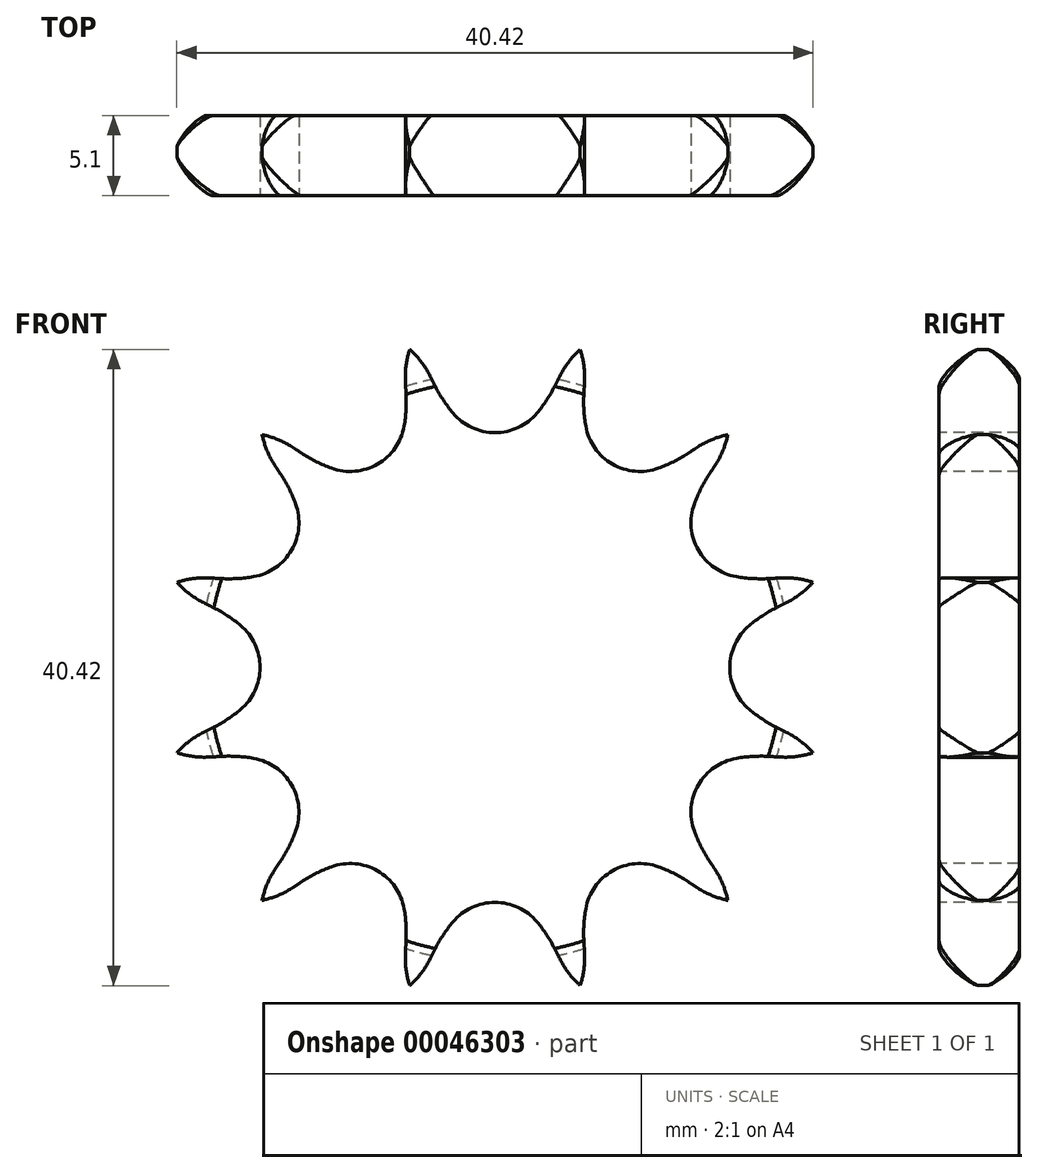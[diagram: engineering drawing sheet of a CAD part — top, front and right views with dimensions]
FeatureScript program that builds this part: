
annotation { "Feature Type Name" : "Feature", "Feature Type Description" : "" }
export const myFeature = defineFeature(function(context is Context, id is Id, definition is map)
    precondition{}
    {
        {
            var Q0;
            Q0=qCreatedBy(makeId("Right.planeOp"),FACE);
            var sketch = newSketch(context, id + "F0", { "sketchPlane" : qUnion([Q0])});
            skLineSegment(sketch, "E0", {"start": v(0, 0) * mm, "end": v(5.1, 0) * mm, "construction": true});
            skLineSegment(sketch, "E1", {"start": v(0, 21) * mm, "end": v(5.1, 21) * mm});
            skLineSegment(sketch, "E2", {"start": v(5.1, 21) * mm, "end": v(5.1, 15) * mm});
            skLineSegment(sketch, "E3", {"start": v(5.1, 15) * mm, "end": v(5.1, 15) * mm});
            skLineSegment(sketch, "E4", {"start": v(5.1, 15) * mm, "end": v(5.1, 0) * mm});
            skLineSegment(sketch, "E5", {"start": v(0, 0) * mm, "end": v(0, 21) * mm});
            skLineSegment(sketch, "E6.0.MirrorCS", {"start": v(0, -21) * mm, "end": v(5.1, -21) * mm});
            skLineSegment(sketch, "E6.1.MirrorCS", {"start": v(5.1, -21) * mm, "end": v(5.1, -15) * mm});
            skLineSegment(sketch, "E6.3.MirrorCS", {"start": v(5.1, -15) * mm, "end": v(5.1, 0) * mm});
            skLineSegment(sketch, "E6.4.MirrorCS", {"start": v(5.1, -15) * mm, "end": v(5.1, -15) * mm});
            skLineSegment(sketch, "E6.5.MirrorCS", {"start": v(0, 0) * mm, "end": v(0, -21) * mm});
            skLineSegment(sketch, "E7", {"start": v(0, 0) * mm, "end": v(5.1, 0) * mm});
            skSolve(sketch);
        }
        {
            var Q0;
            Q0=makeQuery(id+"F0.imprint","IMPRINT",FACE,{"disambiguationData":[TD([[makeQuery(id+"F0.imprint","IMPRINT",EDGE,{"derivedFrom":sQuery(id+"F0.wireOp",EDGE,"E1")}),-1.0]])]});
            var Q1;
            Q1=sQuery(id+"F0.wireOp",EDGE,"E0");
            revolve(context, id + "F1", {"entities" : qUnion([Q0]), "axis" : qUnion([Q1]), "revolveType" : RevolveType.FULL});
        }
        {
            var Q0;
            Q0=makeQuery(id+"F1.opRevolve","SWEPT_EDGE",EDGE,{"disambiguationData":[OSD([sQuery(id+"F0.wireOp",EDGE,"E1"),sQuery(id+"F0.wireOp",EDGE,"E5")])]});
            fillet(context, id + "F2", {"entities" : qUnion([Q0]), "radius" : 2.75 * mm, "tangentPropagation" : true, "rho" : 0.2, "crossSection" : FilletCrossSection.CONIC, "allowEdgeOverflow" : false});
        }
        {
            var Q0;
            Q0=makeQuery(id+"F1.opRevolve","SWEPT_EDGE",EDGE,{"disambiguationData":[OSD([sQuery(id+"F0.wireOp",EDGE,"E1"),sQuery(id+"F0.wireOp",EDGE,"E2")])]});
            fillet(context, id + "F3", {"entities" : qUnion([Q0]), "radius" : 2.25 * mm, "tangentPropagation" : true, "rho" : 0.2, "crossSection" : FilletCrossSection.CONIC, "allowEdgeOverflow" : false});
        }
        {
            var Q0;
            Q0=qCreatedBy(makeId("Front.planeOp"),FACE);
            var sketch = newSketch(context, id + "F4", { "sketchPlane" : qUnion([Q0])});
            skPoint(sketch, "E8.0", {"position": v(0, 0) * mm});
            skArc(sketch, "E9", {"start": v(2.67, 16.16) * mm, "mid": v(0, 21.88) * mm, "end": v(-2.67, 16.16) * mm, "construction": true});
            skLineSegment(sketch, "E10", {"start": v(0, 0) * mm, "end": v(7.32, 0) * mm, "construction": true});
            skArc(sketch, "E11", {"start": v(-2.67, 16.16) * mm, "mid": v(11.7, 26.86) * mm, "end": v(-3.81, 17.9) * mm, "construction": true});
            skLineSegment(sketch, "E12", {"start": v(4.9, 0.57) * mm, "end": v(-4.12, 18.5) * mm, "construction": true});
            skArc(sketch, "E13", {"start": v(-5.41, 20.2) * mm, "mid": v(-13.86, 12.42) * mm, "end": v(-4.12, 18.5) * mm, "construction": true});
            skLineSegment(sketch, "E14", {"start": v(0, 0) * mm, "end": v(-5.41, 20.2) * mm, "construction": true});
            skLineSegment(sketch, "E15", {"start": v(4.2, 21.93) * mm, "end": v(-3.81, 17.9) * mm, "construction": true});
            skLineSegment(sketch, "E16", {"start": v(0, 18.4) * mm, "end": v(4.2, 21.93) * mm, "construction": true});
            skLineSegment(sketch, "E17", {"start": v(0, 18.4) * mm, "end": v(72.06, 18.4) * mm, "construction": true});
            skLineSegment(sketch, "E18", {"start": v(0, 0) * mm, "end": v(0, 18.4) * mm, "construction": true});
            skCircle(sketch, "E19", {"center": v(0, 0) * mm, "radius": 18.4 * mm, "construction": true});
            skArc(sketch, "E20", {"start": v(-2.67, 16.16) * mm, "mid": v(0, 14.92) * mm, "end": v(2.67, 16.16) * mm});
            skArc(sketch, "E21.0.MirrorCS", {"start": v(4.12, 18.5) * mm, "mid": v(4.69, 19.42) * mm, "end": v(5.41, 20.2) * mm});
            skLineSegment(sketch, "E22.0.MirrorCS", {"start": v(3.81, 17.9) * mm, "end": v(4.12, 18.5) * mm});
            skArc(sketch, "E23.0.MirrorCS", {"start": v(3.81, 17.9) * mm, "mid": v(3.3, 17) * mm, "end": v(2.67, 16.16) * mm});
            skArc(sketch, "E24", {"start": v(-3.81, 17.9) * mm, "mid": v(-3.3, 17) * mm, "end": v(-2.67, 16.16) * mm});
            skArc(sketch, "E25", {"start": v(-4.12, 18.5) * mm, "mid": v(-4.69, 19.42) * mm, "end": v(-5.41, 20.2) * mm});
            skLineSegment(sketch, "E26", {"start": v(-3.81, 17.9) * mm, "end": v(-4.12, 18.5) * mm});
            skArc(sketch, "E27.1.0", {"start": v(-12.82, 13.97) * mm, "mid": v(-13.77, 14.47) * mm, "end": v(-14.8, 14.8) * mm});
            skLineSegment(sketch, "E27.1.1", {"start": v(-12.25, 13.6) * mm, "end": v(-12.82, 13.97) * mm});
            skArc(sketch, "E27.1.2", {"start": v(-12.25, 13.6) * mm, "mid": v(-11.35, 13.07) * mm, "end": v(-10.4, 12.66) * mm});
            skArc(sketch, "E27.1.3", {"start": v(-5.65, 17.4) * mm, "mid": v(-5.65, 16.37) * mm, "end": v(-5.77, 15.33) * mm});
            skLineSegment(sketch, "E27.1.4", {"start": v(-5.65, 17.4) * mm, "end": v(-5.69, 18.08) * mm});
            skArc(sketch, "E27.1.5", {"start": v(-5.69, 18.08) * mm, "mid": v(-5.65, 19.16) * mm, "end": v(-5.41, 20.2) * mm});
            skArc(sketch, "E27.1.6", {"start": v(-10.4, 12.66) * mm, "mid": v(-7.46, 12.92) * mm, "end": v(-5.77, 15.33) * mm});
            skArc(sketch, "E27.2.0", {"start": v(-18.08, 5.69) * mm, "mid": v(-19.16, 5.65) * mm, "end": v(-20.2, 5.41) * mm});
            skLineSegment(sketch, "E27.2.1", {"start": v(-17.4, 5.65) * mm, "end": v(-18.08, 5.69) * mm});
            skArc(sketch, "E27.2.2", {"start": v(-17.4, 5.65) * mm, "mid": v(-16.37, 5.65) * mm, "end": v(-15.33, 5.77) * mm});
            skArc(sketch, "E27.2.3", {"start": v(-13.6, 12.25) * mm, "mid": v(-13.07, 11.35) * mm, "end": v(-12.66, 10.4) * mm});
            skLineSegment(sketch, "E27.2.4", {"start": v(-13.6, 12.25) * mm, "end": v(-13.97, 12.82) * mm});
            skArc(sketch, "E27.2.5", {"start": v(-13.97, 12.82) * mm, "mid": v(-14.47, 13.77) * mm, "end": v(-14.8, 14.8) * mm});
            skArc(sketch, "E27.2.6", {"start": v(-15.33, 5.77) * mm, "mid": v(-12.92, 7.46) * mm, "end": v(-12.66, 10.4) * mm});
            skArc(sketch, "E27.3.0", {"start": v(-18.5, -4.12) * mm, "mid": v(-19.42, -4.69) * mm, "end": v(-20.2, -5.41) * mm});
            skLineSegment(sketch, "E27.3.1", {"start": v(-17.9, -3.81) * mm, "end": v(-18.5, -4.12) * mm});
            skArc(sketch, "E27.3.2", {"start": v(-17.9, -3.81) * mm, "mid": v(-17, -3.3) * mm, "end": v(-16.16, -2.67) * mm});
            skArc(sketch, "E27.3.3", {"start": v(-17.9, 3.81) * mm, "mid": v(-17, 3.3) * mm, "end": v(-16.16, 2.67) * mm});
            skLineSegment(sketch, "E27.3.4", {"start": v(-17.9, 3.81) * mm, "end": v(-18.5, 4.12) * mm});
            skArc(sketch, "E27.3.5", {"start": v(-18.5, 4.12) * mm, "mid": v(-19.42, 4.69) * mm, "end": v(-20.2, 5.41) * mm});
            skArc(sketch, "E27.3.6", {"start": v(-16.16, -2.67) * mm, "mid": v(-14.92, 0) * mm, "end": v(-16.16, 2.67) * mm});
            skArc(sketch, "E27.4.0", {"start": v(-13.97, -12.82) * mm, "mid": v(-14.47, -13.77) * mm, "end": v(-14.8, -14.8) * mm});
            skLineSegment(sketch, "E27.4.1", {"start": v(-13.6, -12.25) * mm, "end": v(-13.97, -12.82) * mm});
            skArc(sketch, "E27.4.2", {"start": v(-13.6, -12.25) * mm, "mid": v(-13.07, -11.35) * mm, "end": v(-12.66, -10.4) * mm});
            skArc(sketch, "E27.4.3", {"start": v(-17.4, -5.65) * mm, "mid": v(-16.37, -5.65) * mm, "end": v(-15.33, -5.77) * mm});
            skLineSegment(sketch, "E27.4.4", {"start": v(-17.4, -5.65) * mm, "end": v(-18.08, -5.69) * mm});
            skArc(sketch, "E27.4.5", {"start": v(-18.08, -5.69) * mm, "mid": v(-19.16, -5.65) * mm, "end": v(-20.2, -5.41) * mm});
            skArc(sketch, "E27.4.6", {"start": v(-12.66, -10.4) * mm, "mid": v(-12.92, -7.46) * mm, "end": v(-15.33, -5.77) * mm});
            skArc(sketch, "E27.5.0", {"start": v(-5.69, -18.08) * mm, "mid": v(-5.65, -19.16) * mm, "end": v(-5.41, -20.2) * mm});
            skLineSegment(sketch, "E27.5.1", {"start": v(-5.65, -17.4) * mm, "end": v(-5.69, -18.08) * mm});
            skArc(sketch, "E27.5.2", {"start": v(-5.65, -17.4) * mm, "mid": v(-5.65, -16.37) * mm, "end": v(-5.77, -15.33) * mm});
            skArc(sketch, "E27.5.3", {"start": v(-12.25, -13.6) * mm, "mid": v(-11.35, -13.07) * mm, "end": v(-10.4, -12.66) * mm});
            skLineSegment(sketch, "E27.5.4", {"start": v(-12.25, -13.6) * mm, "end": v(-12.82, -13.97) * mm});
            skArc(sketch, "E27.5.5", {"start": v(-12.82, -13.97) * mm, "mid": v(-13.77, -14.47) * mm, "end": v(-14.8, -14.8) * mm});
            skArc(sketch, "E27.5.6", {"start": v(-5.77, -15.33) * mm, "mid": v(-7.46, -12.92) * mm, "end": v(-10.4, -12.66) * mm});
            skArc(sketch, "E27.6.0", {"start": v(4.12, -18.5) * mm, "mid": v(4.69, -19.42) * mm, "end": v(5.41, -20.2) * mm});
            skLineSegment(sketch, "E27.6.1", {"start": v(3.81, -17.9) * mm, "end": v(4.12, -18.5) * mm});
            skArc(sketch, "E27.6.2", {"start": v(3.81, -17.9) * mm, "mid": v(3.3, -17) * mm, "end": v(2.67, -16.16) * mm});
            skArc(sketch, "E27.6.3", {"start": v(-3.81, -17.9) * mm, "mid": v(-3.3, -17) * mm, "end": v(-2.67, -16.16) * mm});
            skLineSegment(sketch, "E27.6.4", {"start": v(-3.81, -17.9) * mm, "end": v(-4.12, -18.5) * mm});
            skArc(sketch, "E27.6.5", {"start": v(-4.12, -18.5) * mm, "mid": v(-4.69, -19.42) * mm, "end": v(-5.41, -20.2) * mm});
            skArc(sketch, "E27.6.6", {"start": v(2.67, -16.16) * mm, "mid": v(0, -14.92) * mm, "end": v(-2.67, -16.16) * mm});
            skArc(sketch, "E27.7.0", {"start": v(12.82, -13.97) * mm, "mid": v(13.77, -14.47) * mm, "end": v(14.8, -14.8) * mm});
            skLineSegment(sketch, "E27.7.1", {"start": v(12.25, -13.6) * mm, "end": v(12.82, -13.97) * mm});
            skArc(sketch, "E27.7.2", {"start": v(12.25, -13.6) * mm, "mid": v(11.35, -13.07) * mm, "end": v(10.4, -12.66) * mm});
            skArc(sketch, "E27.7.3", {"start": v(5.65, -17.4) * mm, "mid": v(5.65, -16.37) * mm, "end": v(5.77, -15.33) * mm});
            skLineSegment(sketch, "E27.7.4", {"start": v(5.65, -17.4) * mm, "end": v(5.69, -18.08) * mm});
            skArc(sketch, "E27.7.5", {"start": v(5.69, -18.08) * mm, "mid": v(5.65, -19.16) * mm, "end": v(5.41, -20.2) * mm});
            skArc(sketch, "E27.7.6", {"start": v(10.4, -12.66) * mm, "mid": v(7.46, -12.92) * mm, "end": v(5.77, -15.33) * mm});
            skArc(sketch, "E27.8.0", {"start": v(18.08, -5.69) * mm, "mid": v(19.16, -5.65) * mm, "end": v(20.2, -5.41) * mm});
            skLineSegment(sketch, "E27.8.1", {"start": v(17.4, -5.65) * mm, "end": v(18.08, -5.69) * mm});
            skArc(sketch, "E27.8.2", {"start": v(17.4, -5.65) * mm, "mid": v(16.37, -5.65) * mm, "end": v(15.33, -5.77) * mm});
            skArc(sketch, "E27.8.3", {"start": v(13.6, -12.25) * mm, "mid": v(13.07, -11.35) * mm, "end": v(12.66, -10.4) * mm});
            skLineSegment(sketch, "E27.8.4", {"start": v(13.6, -12.25) * mm, "end": v(13.97, -12.82) * mm});
            skArc(sketch, "E27.8.5", {"start": v(13.97, -12.82) * mm, "mid": v(14.47, -13.77) * mm, "end": v(14.8, -14.8) * mm});
            skArc(sketch, "E27.8.6", {"start": v(15.33, -5.77) * mm, "mid": v(12.92, -7.46) * mm, "end": v(12.66, -10.4) * mm});
            skArc(sketch, "E27.9.0", {"start": v(18.5, 4.12) * mm, "mid": v(19.42, 4.69) * mm, "end": v(20.2, 5.41) * mm});
            skLineSegment(sketch, "E27.9.1", {"start": v(17.9, 3.81) * mm, "end": v(18.5, 4.12) * mm});
            skArc(sketch, "E27.9.2", {"start": v(17.9, 3.81) * mm, "mid": v(17, 3.3) * mm, "end": v(16.16, 2.67) * mm});
            skArc(sketch, "E27.9.3", {"start": v(17.9, -3.81) * mm, "mid": v(17, -3.3) * mm, "end": v(16.16, -2.67) * mm});
            skLineSegment(sketch, "E27.9.4", {"start": v(17.9, -3.81) * mm, "end": v(18.5, -4.12) * mm});
            skArc(sketch, "E27.9.5", {"start": v(18.5, -4.12) * mm, "mid": v(19.42, -4.69) * mm, "end": v(20.2, -5.41) * mm});
            skArc(sketch, "E27.9.6", {"start": v(16.16, 2.67) * mm, "mid": v(14.92, 0) * mm, "end": v(16.16, -2.67) * mm});
            skArc(sketch, "E27.10.0", {"start": v(13.97, 12.82) * mm, "mid": v(14.47, 13.77) * mm, "end": v(14.8, 14.8) * mm});
            skLineSegment(sketch, "E27.10.1", {"start": v(13.6, 12.25) * mm, "end": v(13.97, 12.82) * mm});
            skArc(sketch, "E27.10.2", {"start": v(13.6, 12.25) * mm, "mid": v(13.07, 11.35) * mm, "end": v(12.66, 10.4) * mm});
            skArc(sketch, "E27.10.3", {"start": v(17.4, 5.65) * mm, "mid": v(16.37, 5.65) * mm, "end": v(15.33, 5.77) * mm});
            skLineSegment(sketch, "E27.10.4", {"start": v(17.4, 5.65) * mm, "end": v(18.08, 5.69) * mm});
            skArc(sketch, "E27.10.5", {"start": v(18.08, 5.69) * mm, "mid": v(19.16, 5.65) * mm, "end": v(20.2, 5.41) * mm});
            skArc(sketch, "E27.10.6", {"start": v(12.66, 10.4) * mm, "mid": v(12.92, 7.46) * mm, "end": v(15.33, 5.77) * mm});
            skArc(sketch, "E27.11.0", {"start": v(5.69, 18.08) * mm, "mid": v(5.65, 19.16) * mm, "end": v(5.41, 20.2) * mm});
            skLineSegment(sketch, "E27.11.1", {"start": v(5.65, 17.4) * mm, "end": v(5.69, 18.08) * mm});
            skArc(sketch, "E27.11.2", {"start": v(5.65, 17.4) * mm, "mid": v(5.65, 16.37) * mm, "end": v(5.77, 15.33) * mm});
            skArc(sketch, "E27.11.3", {"start": v(12.25, 13.6) * mm, "mid": v(11.35, 13.07) * mm, "end": v(10.4, 12.66) * mm});
            skLineSegment(sketch, "E27.11.4", {"start": v(12.25, 13.6) * mm, "end": v(12.82, 13.97) * mm});
            skArc(sketch, "E27.11.5", {"start": v(12.82, 13.97) * mm, "mid": v(13.77, 14.47) * mm, "end": v(14.8, 14.8) * mm});
            skArc(sketch, "E27.11.6", {"start": v(5.77, 15.33) * mm, "mid": v(7.46, 12.92) * mm, "end": v(10.4, 12.66) * mm});
            skSolve(sketch);
        }
        {
            var Q0;
            Q0 = qSketchRegion(id + "F4", true);
            extrude(context, id + "F5", {"entities" : qUnion([Q0]), "operationType" : NewBodyOperationType.INTERSECT, "endBound" : BoundingType.THROUGH_ALL, "oppositeDirection" : true, "depth" : 25.4 * mm});
        }
    });
